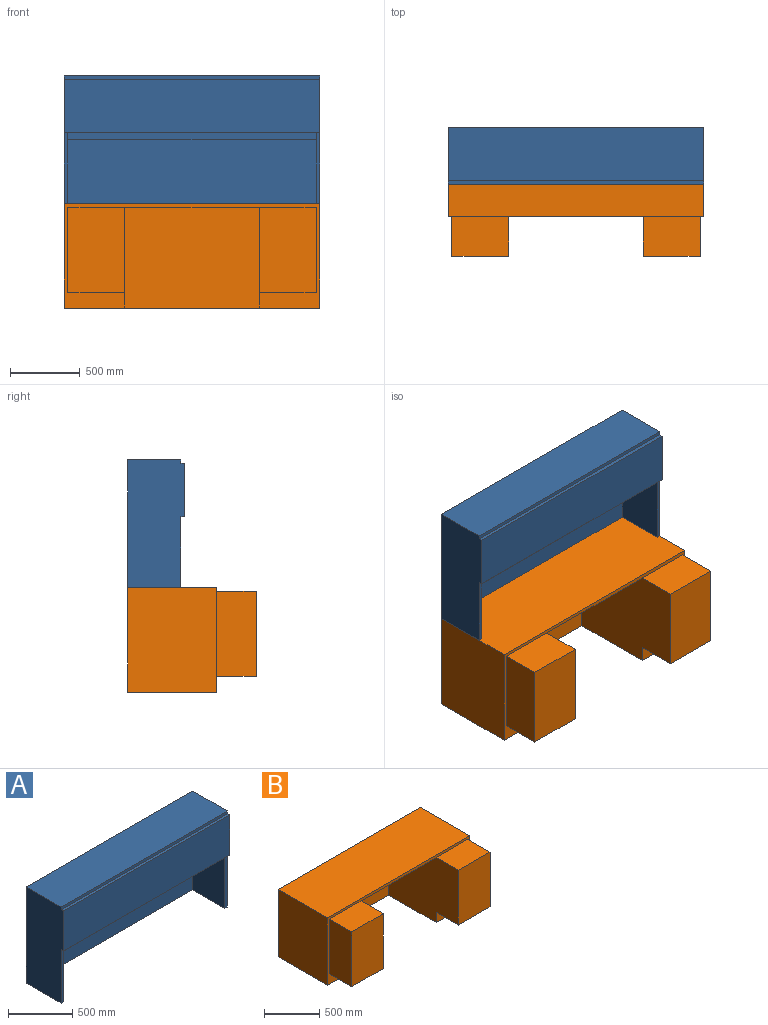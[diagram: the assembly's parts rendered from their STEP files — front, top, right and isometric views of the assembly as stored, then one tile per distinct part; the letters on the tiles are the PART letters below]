
ASSEMBLY  parts=2 mates=1
PART A: 18 faces, bbox 1828.8x406.4x914.4 mm
  f0: plane 1778x25.4mm, normal (0,0,-1), area 45161.2mm2, adj f12,f13,f14,f17
  f1: plane 1828.8x381mm, normal (0,-1,0), area 696772.8mm2, adj f3,f4,f8,f10
  f2: plane 1828.8x381mm, normal (0,0,-1), area 64516mm2, adj f3,f4,f6,f7,f9,f12,f13,f15
  f3: plane 914.4x406.4mm, normal (1,0,0), area 358063.8mm2, adj f1,f2,f5,f6,f8,f9,f10,f11
  f4: plane 914.4x406.4mm, normal (-1,0,0), area 358063.8mm2, adj f1,f2,f5,f6,f7,f8,f10,f11
  f5: plane 1828.8x381mm, normal (0,0,1), area 696772.8mm2, adj f3,f4,f6,f11
  f6: plane 1828.8x914.4mm, normal (0,1,0), area 1672254.7mm2, adj f2,f3,f4,f5
  f7: plane 508x25.4mm, normal (0,-1,0), area 12903.2mm2, adj f2,f4,f8,f12
  f8: plane 1828.8x50.8mm, normal (0,0,-1), area 91612.7mm2, adj f1,f3,f4,f7,f9,f12,f13,f14
  f9: plane 508x25.4mm, normal (0,-1,0), area 12903.2mm2, adj f2,f3,f8,f13
  f10: plane 1828.8x25.4mm, normal (0,0,1), area 46451.5mm2, adj f1,f3,f4,f11
  f11: plane 1828.8x25.4mm, normal (0,-1,0), area 46451.5mm2, adj f3,f4,f5,f10
  f12: plane 508x355.6mm, normal (1,0,0), area 179354.5mm2, adj f0,f2,f7,f8,f14,f15,f16,f17
  f13: plane 508x355.6mm, normal (-1,0,0), area 179354.5mm2, adj f0,f2,f8,f9,f14,f15,f16,f17
  f14: plane 1778x50.8mm, normal (0,-1,0), area 90322.4mm2, adj f0,f8,f12,f13
  f15: plane 1778x508mm, normal (0,-1,0), area 903224mm2, adj f2,f12,f13,f16
  f16: plane 1778x304.8mm, normal (0,0,-1), area 541934.4mm2, adj f12,f13,f15,f17
  f17: plane 1778x50.8mm, normal (0,1,0), area 90322.4mm2, adj f0,f12,f13,f16
PART B: 18 faces, bbox 1828.8x920.8x749.3 mm
  f0: plane 1828.8x749.3mm, normal (0,-1,0), area 176128.7mm2, adj f1,f2,f3,f4,f6,f7,f8,f10
  f1: plane 1828.8x635mm, normal (0,0,-1), area 572902.1mm2, adj f0,f2,f3,f5,f6,f7,f9
  f2: plane 749.3x635mm, normal (-1,0,0), area 475805.5mm2, adj f0,f1,f4,f5
  f3: plane 749.3x635mm, normal (1,0,0), area 475805.5mm2, adj f0,f1,f4,f5
  f4: plane 1828.8x635mm, normal (0,0,1), area 1161288mm2, adj f0,f2,f3,f5
  f5: plane 1828.8x749.3mm, normal (0,1,0), area 1370319.8mm2, adj f1,f2,f3,f4
  f6: plane 895.35x723.9mm, normal (1,0,0), area 615482.6mm2, adj f0,f1,f8,f9,f10,f11,f13
  f7: plane 895.35x723.9mm, normal (-1,0,0), area 615482.6mm2, adj f0,f1,f8,f9,f14,f16,f17
  f8: plane 965.2x609.6mm, normal (0,0,-1), area 588385.9mm2, adj f0,f6,f7,f9
  f9: plane 965.2x723.9mm, normal (0,-1,0), area 698708.3mm2, adj f1,f6,f7,f8
  f10: plane 406.4x285.75mm, normal (0,0,-1), area 116128.8mm2, adj f0,f6,f12,f13
  f11: plane 406.4x285.75mm, normal (0,0,1), area 116128.8mm2, adj f0,f6,f12,f13
  f12: plane 609.6x285.75mm, normal (-1,0,0), area 174193.2mm2, adj f0,f10,f11,f13
  f13: plane 609.6x406.4mm, normal (0,-1,0), area 247741.4mm2, adj f6,f10,f11,f12
  f14: plane 406.4x285.75mm, normal (0,0,-1), area 116128.8mm2, adj f0,f7,f15,f17
  f15: plane 609.6x285.75mm, normal (1,0,0), area 174193.2mm2, adj f0,f14,f16,f17
  f16: plane 406.4x285.75mm, normal (0,0,1), area 116128.8mm2, adj f0,f7,f15,f17
  f17: plane 609.6x406.4mm, normal (0,-1,0), area 247741.4mm2, adj f7,f14,f15,f16
PLACE A t=(0,228.6,749.3)mm
PLACE B at identity
MATE fastened A.f2 <-> B.f4  axis (0,0,1) through (1828.8,635,749.3)mm
